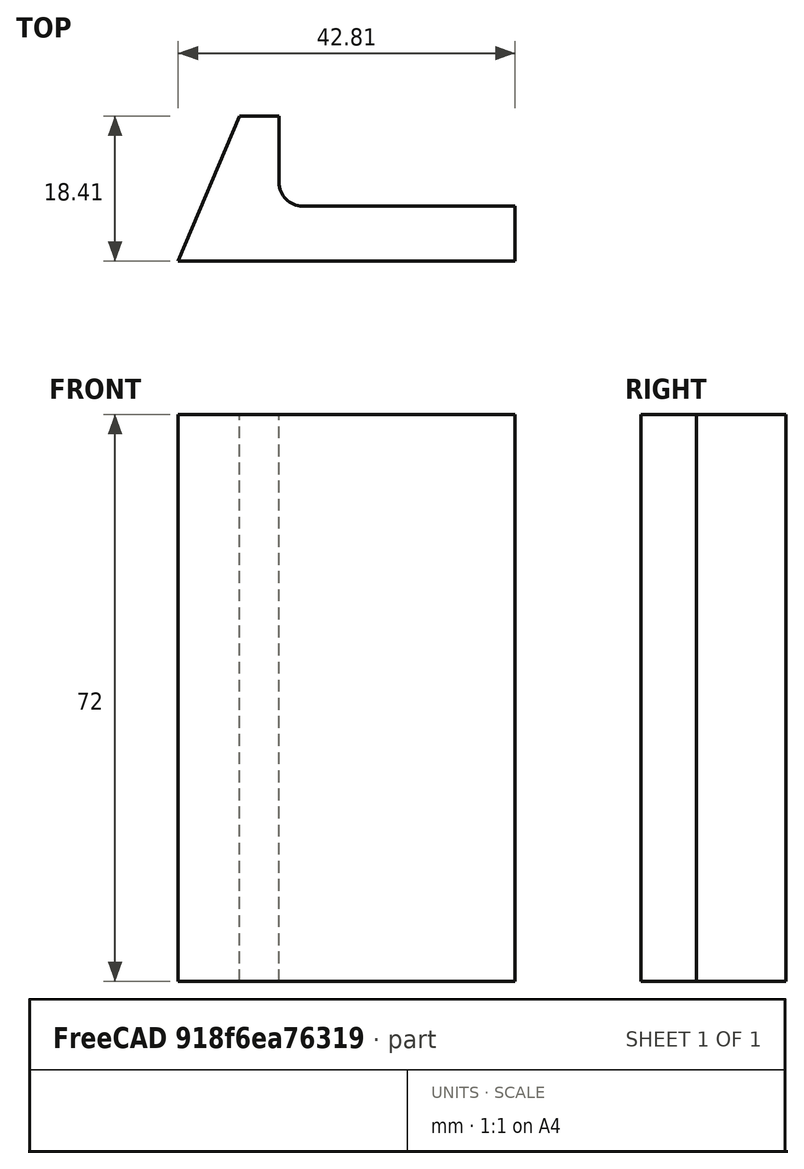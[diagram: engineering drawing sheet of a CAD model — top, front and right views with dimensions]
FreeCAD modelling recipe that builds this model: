
FCSTD DOCUMENT  (FreeCAD 1.0R39109 (Git))
Label: LimelightMount
License: All rights reserved
LicenseURL: https://en.wikipedia.org/wiki/All_rights_reserved
objects: Sketcher::SketchObject×1, PartDesign::Pad×1, PartDesign::Body×1
note: 6 computed .brp shape members not serialized (recipe doc carries the construction recipe); baked Part::Feature solids carry a one-line shape summary decoded from their .brp

FEATURE [Sketcher::SketchObject] Sketch
  ArcFitTolerance = 1e-06
  AttachmentSupport = -> [XY_Plane]
  FullyConstrained = true
  MakeInternals = false
  MapMode = 5
  sketch-geometry (8):
    g0: LineSegment StartX=-2.6859e-12 StartY=1.886e-13 StartZ=0 EndX=7.81462 EndY=18.4101 EndZ=0
    g1: LineSegment StartX=7.81462 StartY=18.4101 StartZ=0 EndX=12.8146 EndY=18.4101 EndZ=0
    g2: LineSegment StartX=12.8146 StartY=18.4101 StartZ=0 EndX=12.8146 EndY=10 EndZ=0
    g3: LineSegment StartX=15.8146 StartY=7 StartZ=0 EndX=42.8146 EndY=7 EndZ=0
    g4: LineSegment StartX=42.8146 StartY=7 StartZ=0 EndX=42.8146 EndY=-9e-16 EndZ=0
    g5: LineSegment StartX=42.8146 StartY=-9e-16 StartZ=0 EndX=-2.6859e-12 EndY=1.886e-13 EndZ=0
    g6: ArcOfCircle CenterX=15.8146 CenterY=10 CenterZ=0 NormalX=0 NormalY=0 NormalZ=1 AngleXU=0 Radius=3 StartAngle=3.14159 EndAngle=4.71239
    g7: GeomPoint [constr] X=12.8146 Y=7 Z=0
  constraints (21):
    c: Coincident(g0,g-1)
    c: Angle(g-2,g0) = 2.74017
    c: Distance(g1) = 5
    c: Coincident(g1,g0)
    c: Horizontal(g1)
    c: Coincident(g2,g1)
    c: Vertical(g2)
    c: Distance(g3,g7) = 30
    c: Horizontal(g3)
    c: Coincident(g4,g3)
    c: PointOnObject(g4,g-1)
    c: Vertical(g4)
    c: Coincident(g5,g4)
    c: Coincident(g5,g0)
    c: Distance(g0,g0) = 20
    c: DistanceY(g4,g4) = 7
    c: PointOnObject(g7,g2)
    c: PointOnObject(g7,g3)
    c: Tangent(g2,g6) = -1.5708
    c: Tangent(g3,g6) = -1.5708
    c: Radius(g6) = 3
FEATURE [PartDesign::Pad] Pad
  Direction = (0,0,1)
  Length = 72
  Length2 = 10
  Profile = -> Sketch
  ReferenceAxis = -> Sketch [N_Axis]
  Refine = true
  Suppressed = false
  Type = 0
FEATURE [PartDesign::Body] Body  label="Limelight mount"
  AllowCompound = true
  Group = -> [Sketch,Pad]
  Origin = -> Origin
  Tip = -> Pad
